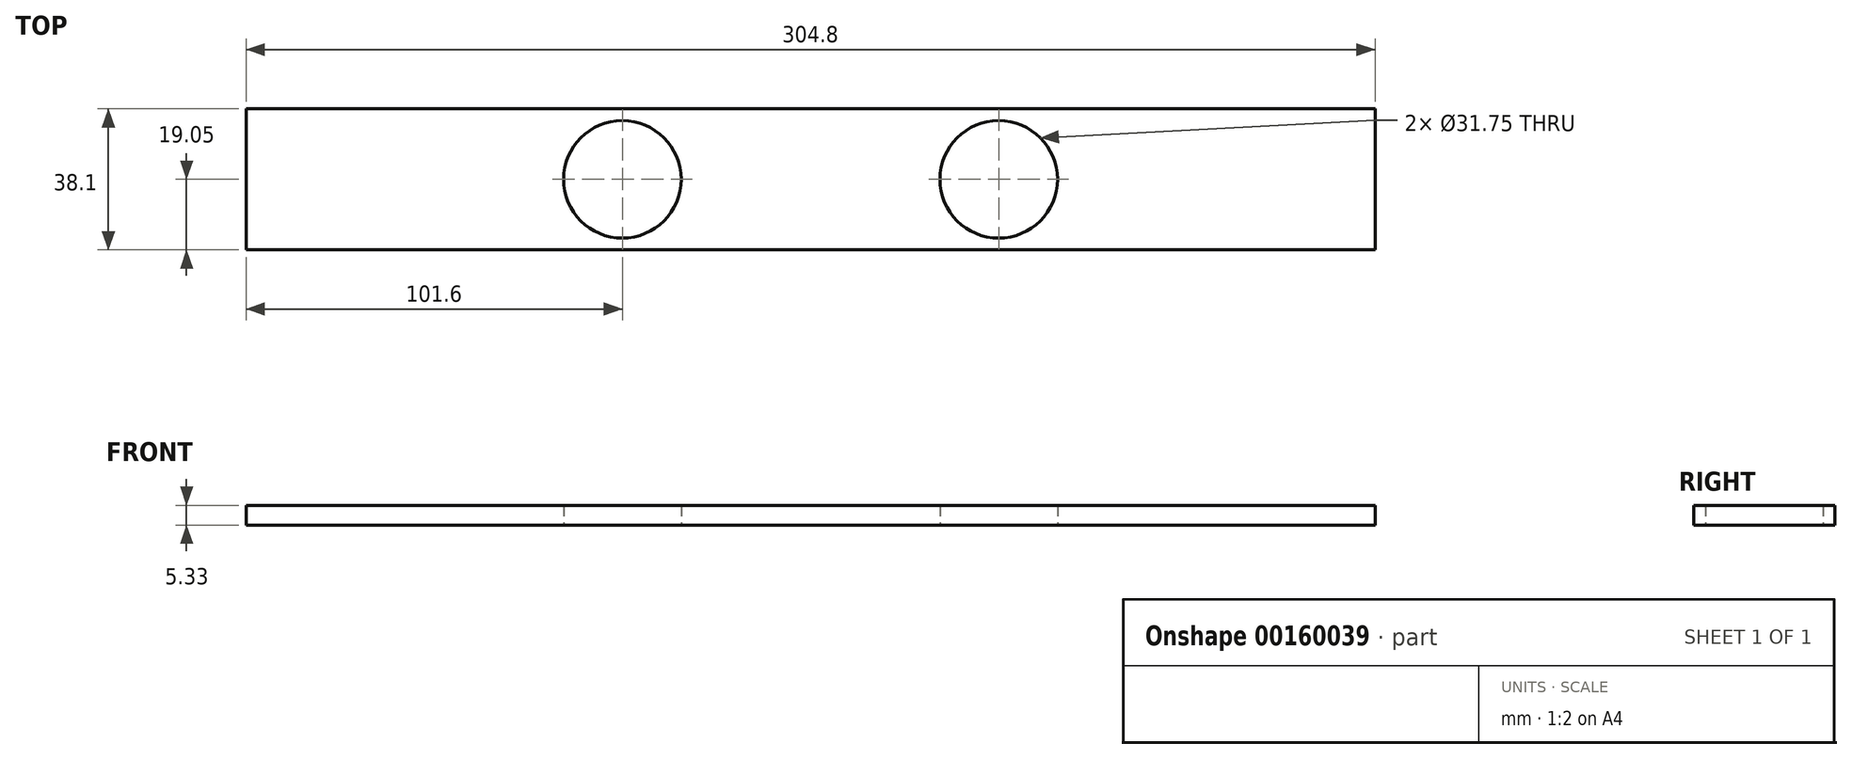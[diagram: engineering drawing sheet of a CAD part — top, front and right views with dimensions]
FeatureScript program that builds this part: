
annotation { "Feature Type Name" : "Feature", "Feature Type Description" : "" }
export const myFeature = defineFeature(function(context is Context, id is Id, definition is map)
    precondition{}
    {
        {
            var Q0;
            Q0=qCreatedBy(makeId("Top.planeOp"),FACE);
            var sketch = newSketch(context, id + "F0", { "sketchPlane" : qUnion([Q0])});
            skLineSegment(sketch, "E0.bottom", {"start": v(0, 0) * mm, "end": v(304.8, 0) * mm});
            skLineSegment(sketch, "E0.top", {"start": v(0, 38.1) * mm, "end": v(304.8, 38.1) * mm});
            skLineSegment(sketch, "E0.left", {"start": v(0, 0) * mm, "end": v(0, 38.1) * mm});
            skLineSegment(sketch, "E0.right", {"start": v(304.8, 0) * mm, "end": v(304.8, 38.1) * mm});
            skCircle(sketch, "E1", {"center": v(101.6, 19.05) * mm, "radius": 15.88 * mm});
            skCircle(sketch, "E2", {"center": v(203.2, 19.05) * mm, "radius": 15.88 * mm});
            skSolve(sketch);
        }
        {
            var Q0;
            Q0 = qSketchRegion(id + "F0", true);
            extrude(context, id + "F1", {"entities" : qUnion([Q0]), "depth" : 5.33 * mm});
        }
    });
